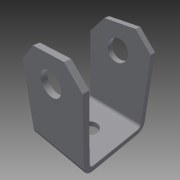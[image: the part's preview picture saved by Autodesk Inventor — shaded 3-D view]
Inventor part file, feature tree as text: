
AUTODESK INVENTOR PART (.ipt)
format: ipt  version: 2015 (Build 190159000, 159)  size: 114,176 bytes
history: native  units: in
note: dims shown in document units (in); Inventor stores cm internally (conversion verified against a paired STEP export)
features: chamfer x1, other x1, imported_body x1
ambient origin geometry x8: Origin, YZ Plane, XZ Plane, XY Plane, X Axis, Y Axis, Z Axis, Center Point
bodies: Body1 (feature_tree)
feature tree (3):
  chamfer  "Chamfer1"  [1 undecoded]
  other  "VL-PNEU-BRK-0011"
  imported_body  "Base1"
note: 1 required parameter value undecoded (feature->parameter linkage not recoverable at this tier; creation-order binding heuristic only, values carry confidence <= 0.55)
